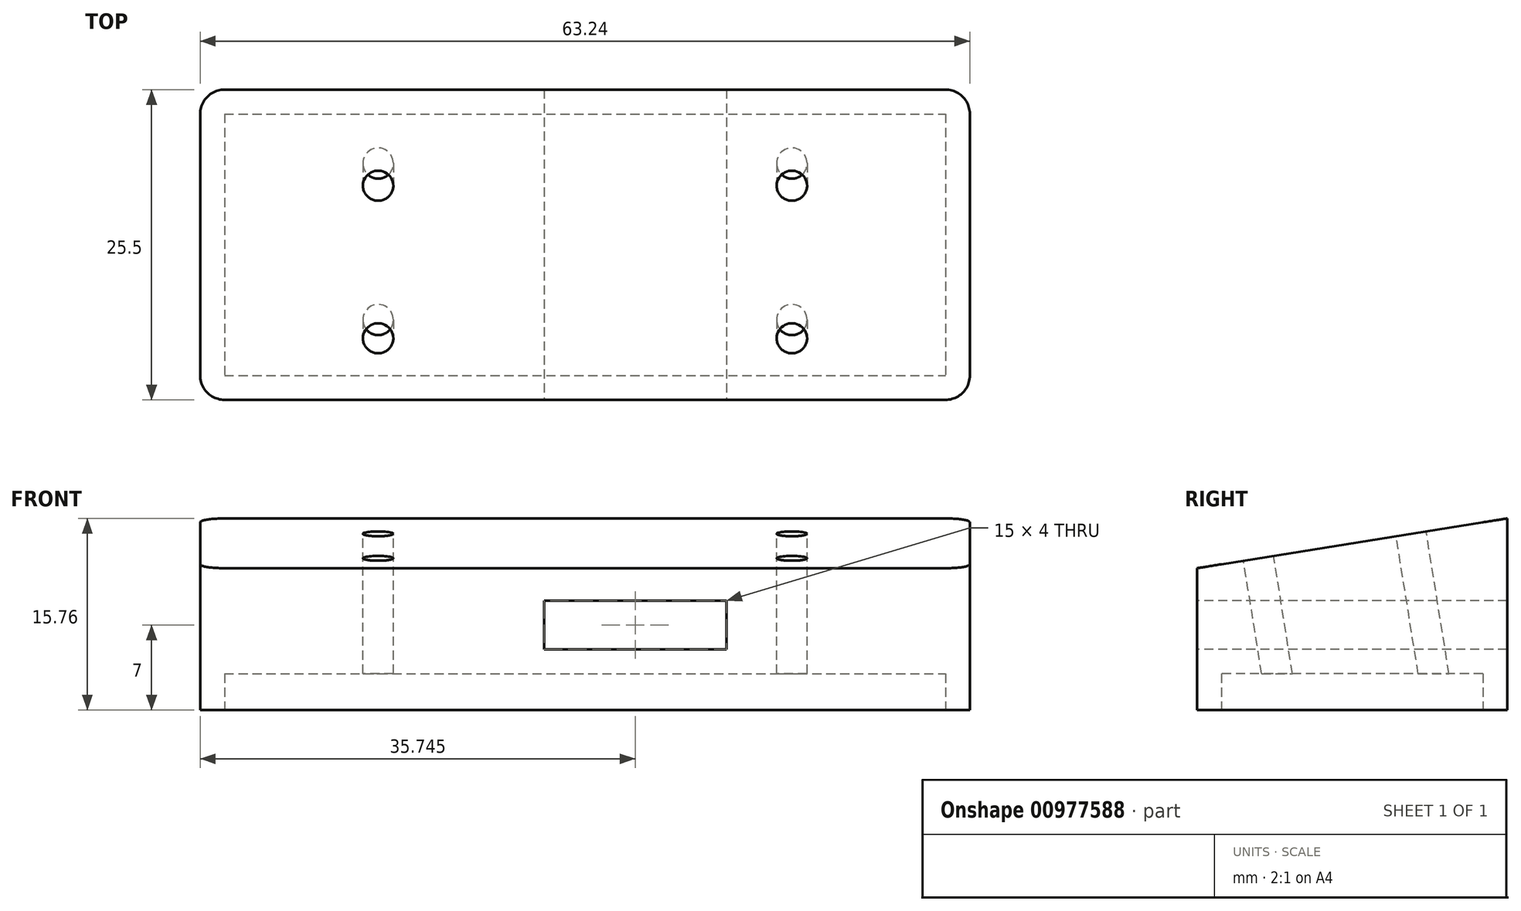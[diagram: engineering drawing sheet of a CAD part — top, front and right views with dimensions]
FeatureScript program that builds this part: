
annotation { "Feature Type Name" : "Feature", "Feature Type Description" : "" }
export const myFeature = defineFeature(function(context is Context, id is Id, definition is map)
    precondition{}
    {
        {
            var Q0;
            Q0=qCreatedBy(makeId("Top.planeOp"),FACE);
            var sketch = newSketch(context, id + "F0", { "sketchPlane" : qUnion([Q0])});
            skLineSegment(sketch, "E0.bottom", {"start": v(-29.63, 10.75) * mm, "end": v(29.63, 10.75) * mm});
            skLineSegment(sketch, "E0.top", {"start": v(-29.63, -10.75) * mm, "end": v(29.63, -10.75) * mm});
            skLineSegment(sketch, "E0.left", {"start": v(-29.63, 10.75) * mm, "end": v(-29.63, -10.75) * mm});
            skLineSegment(sketch, "E0.right", {"start": v(29.63, 10.75) * mm, "end": v(29.63, -10.75) * mm});
            skPoint(sketch, "E0.middle", {"position": v(0, 0) * mm});
            skLineSegment(sketch, "E1.0", {"start": v(-31.63, 12.75) * mm, "end": v(31.63, 12.75) * mm});
            skLineSegment(sketch, "E1.1", {"start": v(-31.63, 12.75) * mm, "end": v(-31.63, -12.75) * mm});
            skLineSegment(sketch, "E1.2", {"start": v(-31.63, -12.75) * mm, "end": v(31.62, -12.75) * mm});
            skLineSegment(sketch, "E1.3", {"start": v(31.63, 12.75) * mm, "end": v(31.62, -12.75) * mm});
            skSolve(sketch);
        }
        {
            var Q0;
            Q0 = qSketchRegion(id + "F0", true);
            var Q1;
            Q1=makeQuery(id+"F0.imprint","IMPRINT",FACE,{"disambiguationData":[TD([[makeQuery(id+"F0.imprint","IMPRINT",EDGE,{"derivedFrom":sQuery(id+"F0.wireOp",EDGE,"E0.bottom")}),-1.0]])]});
            extrude(context, id + "F1", {"entities" : qUnion([Q0, Q1]), "depth" : 20 * mm, "offsetDistance" : 25 * mm});
        }
        {
            var Q0;
            Q0=makeQuery(id+"F1.opExtrude","SWEPT_FACE",FACE,{"disambiguationData":[OSD([sQuery(id+"F0.wireOp",EDGE,"E1.3")])]});
            var sketch = newSketch(context, id + "F2", { "sketchPlane" : qUnion([Q0])});
            skLineSegment(sketch, "E2", {"start": v(12.75, 20) * mm, "end": v(-12.75, 15.95) * mm});
            skLineSegment(sketch, "E3", {"start": v(12.75, 15.97) * mm, "end": v(-12.75, 11.92) * mm});
            skSolve(sketch);
        }
        {
            var Q0;
            Q0=makeQuery(id+"F0.imprint","IMPRINT",FACE,{"disambiguationData":[TD([[makeQuery(id+"F0.imprint","IMPRINT",EDGE,{"derivedFrom":sQuery(id+"F0.wireOp",EDGE,"E0.bottom")}),-1.0]])]});
            extrude(context, id + "F3", {"entities" : qUnion([Q0]), "operationType" : NewBodyOperationType.REMOVE, "depth" : 3 * mm, "offsetDistance" : 25 * mm});
        }
        {
            var Q0;
            Q0 = qSketchRegion(id + "F2", true);
            var Q1;
            {var subQ0=sQuery(id+"F2.wireOp",EDGE,"E2");Q1=makeQuery(id+"F2.imprint","IMPRINT",FACE,{"disambiguationData":[TD([[makeQuery(id+"F2.imprint","IMPRINT",EDGE,{"derivedFrom":subQ0}),-1.0]])]});}
            extrude(context, id + "F4", {"entities" : qUnion([Q0, Q1]), "operationType" : NewBodyOperationType.REMOVE, "oppositeDirection" : true, "depth" : 64 * mm, "offsetDistance" : 25 * mm});
        }
        {
            var Q0;
            Q0=makeQuery(id+"F1.opExtrude","SWEPT_FACE",FACE,{"disambiguationData":[OSD([sQuery(id+"F0.wireOp",EDGE,"E1.2")])]});
            var sketch = newSketch(context, id + "F5", { "sketchPlane" : qUnion([Q0])});
            skLineSegment(sketch, "E4", {"start": v(-3.38, 9) * mm, "end": v(-3.38, 5) * mm});
            skLineSegment(sketch, "E5", {"start": v(-3.38, 5) * mm, "end": v(11.62, 5) * mm});
            skLineSegment(sketch, "E6", {"start": v(11.62, 5) * mm, "end": v(11.62, 9) * mm});
            skLineSegment(sketch, "E7", {"start": v(11.62, 9) * mm, "end": v(-3.38, 9) * mm});
            skSolve(sketch);
        }
        {
            var Q0;
            Q0 = qSketchRegion(id + "F5", true);
            extrude(context, id + "F6", {"entities" : qUnion([Q0]), "operationType" : NewBodyOperationType.REMOVE, "oppositeDirection" : true, "depth" : 30 * mm, "offsetDistance" : 25 * mm});
        }
        {
            var Q0;
            Q0=makeQuery(id+"F1.opExtrude","SWEPT_FACE",FACE,{"disambiguationData":[OSD([sQuery(id+"F0.wireOp",EDGE,"E1.3")])]});
            var sketch = newSketch(context, id + "F7", { "sketchPlane" : qUnion([Q0])});
            skLineSegment(sketch, "E8", {"start": v(12.75, 15.76) * mm, "end": v(-12.75, 11.67) * mm});
            skLineSegment(sketch, "E9", {"start": v(-12.75, 11.67) * mm, "end": v(-12.75, 15.95) * mm});
            skLineSegment(sketch, "E10", {"start": v(-12.75, 15.95) * mm, "end": v(12.75, 20) * mm});
            skLineSegment(sketch, "E11", {"start": v(12.75, 20) * mm, "end": v(12.75, 15.76) * mm});
            skLineSegment(sketch, "E12", {"start": v(12.75, 15.76) * mm, "end": v(-0.7, 15.76) * mm, "construction": true});
            skSolve(sketch);
        }
        {
            var Q0;
            Q0=makeQuery(id+"F7.imprint","IMPRINT",FACE,{"disambiguationData":[TD([[makeQuery(id+"F7.imprint","IMPRINT",EDGE,{"derivedFrom":sQuery(id+"F7.wireOp",EDGE,"E8")}),-1.0]])]});
            extrude(context, id + "F8", {"entities" : qUnion([Q0]), "operationType" : NewBodyOperationType.REMOVE, "oppositeDirection" : true, "depth" : 70 * mm, "offsetDistance" : 25 * mm});
        }
        {
            var Q0;
            Q0=makeQuery(id+"F1.opExtrude","SWEPT_EDGE",EDGE,{"disambiguationData":[OSD([sQuery(id+"F0.wireOp",EDGE,"E1.0"),sQuery(id+"F0.wireOp",EDGE,"E1.1")])]});
            var Q1;
            Q1=makeQuery(id+"F1.opExtrude","SWEPT_EDGE",EDGE,{"disambiguationData":[OSD([sQuery(id+"F0.wireOp",EDGE,"E1.0"),sQuery(id+"F0.wireOp",EDGE,"E1.3")])]});
            var Q2;
            Q2=makeQuery(id+"F1.opExtrude","SWEPT_EDGE",EDGE,{"disambiguationData":[OSD([sQuery(id+"F0.wireOp",EDGE,"E1.1"),sQuery(id+"F0.wireOp",EDGE,"E1.2")])]});
            var Q3;
            Q3=makeQuery(id+"F1.opExtrude","SWEPT_EDGE",EDGE,{"disambiguationData":[OSD([sQuery(id+"F0.wireOp",EDGE,"E1.2"),sQuery(id+"F0.wireOp",EDGE,"E1.3")])]});
            fillet(context, id + "F9", {"entities" : qUnion([Q0, Q1, Q2, Q3]), "radius" : 2 * mm, "tangentPropagation" : true, "allowEdgeOverflow" : false});
        }
        {
            var Q0;
            Q0=makeQuery(id+"F8.boolean.opBoolean","COPY",FACE,{"derivedFrom":makeQuery(id+"F8.opExtrude","SWEPT_FACE",FACE,{"disambiguationData":[OSD([sQuery(id+"F7.wireOp",EDGE,"E8")])]})});
            var sketch = newSketch(context, id + "F10", { "sketchPlane" : qUnion([Q0])});
            skLineSegment(sketch, "E13", {"start": v(0, 15.1) * mm, "end": v(0, -19.57) * mm, "construction": true});
            skLineSegment(sketch, "E14", {"start": v(-17, 16.54) * mm, "end": v(-17, -19.97) * mm, "construction": true});
            skLineSegment(sketch, "E15", {"start": v(17, 15.33) * mm, "end": v(17, -22.7) * mm, "construction": true});
            skLineSegment(sketch, "E16", {"start": v(-27.52, 7.09) * mm, "end": v(27.44, 7.09) * mm, "construction": true});
            skLineSegment(sketch, "E17", {"start": v(-26.79, -5.61) * mm, "end": v(26.7, -5.61) * mm, "construction": true});
            skCircle(sketch, "E18", {"center": v(-17, 7.09) * mm, "radius": 1.25 * mm});
            skCircle(sketch, "E19", {"center": v(-17, -5.61) * mm, "radius": 1.25 * mm});
            skPoint(sketch, "E19.centerSnap0", {"position": v(-17, -1.72) * mm});
            skCircle(sketch, "E20", {"center": v(17, 7.09) * mm, "radius": 1.25 * mm});
            skCircle(sketch, "E21", {"center": v(17, -5.61) * mm, "radius": 1.25 * mm});
            skSolve(sketch);
        }
        {
            var Q0;
            Q0 = qSketchRegion(id + "F10", true);
            extrude(context, id + "F11", {"entities" : qUnion([Q0]), "operationType" : NewBodyOperationType.REMOVE, "oppositeDirection" : true, "depth" : 25 * mm, "offsetDistance" : 25 * mm});
        }
    });
